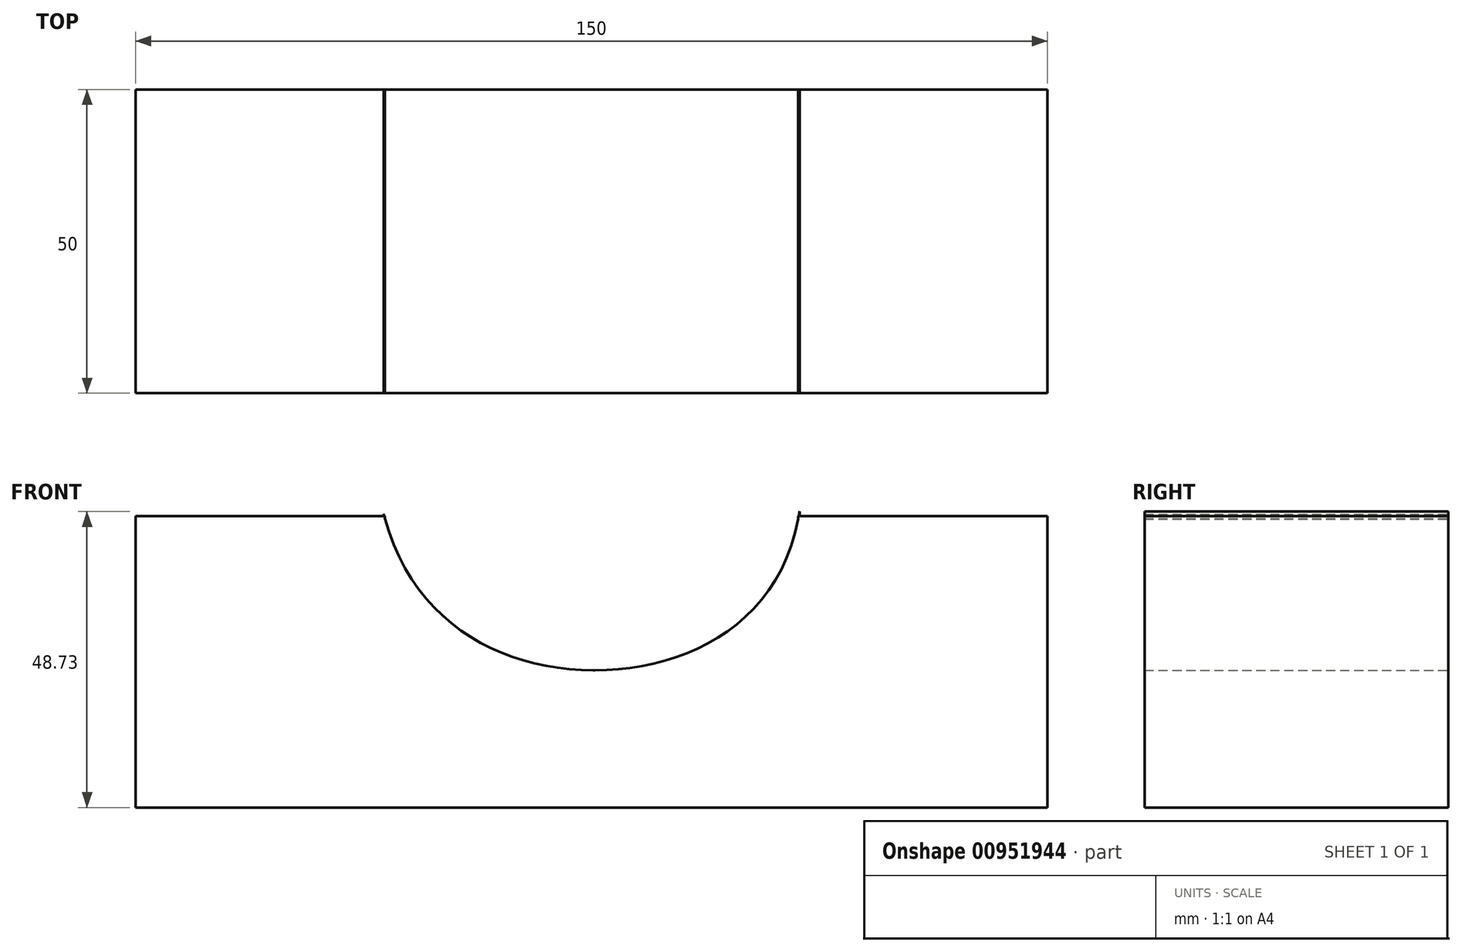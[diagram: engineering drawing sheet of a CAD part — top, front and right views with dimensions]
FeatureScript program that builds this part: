
annotation { "Feature Type Name" : "Feature", "Feature Type Description" : "" }
export const myFeature = defineFeature(function(context is Context, id is Id, definition is map)
    precondition{}
    {
        {
            var Q0;
            Q0=qCreatedBy(makeId("Front.planeOp"),FACE);
            var sketch = newSketch(context, id + "F0", { "sketchPlane" : qUnion([Q0])});
            skLineSegment(sketch, "E0", {"start": v(-75.26, 25.41) * mm, "end": v(-75.26, -22.59) * mm});
            skLineSegment(sketch, "E1", {"start": v(-75.26, -22.59) * mm, "end": v(74.74, -22.59) * mm});
            skLineSegment(sketch, "E2", {"start": v(74.74, -22.59) * mm, "end": v(74.74, 25.41) * mm});
            skLineSegment(sketch, "E3", {"start": v(74.74, 25.41) * mm, "end": v(33.74, 25.41) * mm});
            skLineSegment(sketch, "E4", {"start": v(33.74, 25.41) * mm, "end": v(33.74, 0) * mm});
            skLineSegment(sketch, "E5", {"start": v(33.74, 0) * mm, "end": v(-34.26, 0) * mm});
            skLineSegment(sketch, "E6", {"start": v(-34.26, 0) * mm, "end": v(-34.26, 25.41) * mm});
            skLineSegment(sketch, "E7", {"start": v(-34.26, 25.41) * mm, "end": v(-75.26, 25.41) * mm});
            skSolve(sketch);
        }
        {
            var Q0;
            Q0=makeQuery(id+"F0.imprint","IMPRINT",FACE,{"disambiguationData":[TD([[makeQuery(id+"F0.imprint","IMPRINT",EDGE,{"derivedFrom":sQuery(id+"F0.wireOp",EDGE,"E0")}),1.0]])]});
            extrude(context, id + "F1", {"entities" : qUnion([Q0]), "depth" : 50 * mm, "offsetDistance" : 25 * mm});
        }
        {
            var Q0;
            Q0=qCreatedBy(makeId("Front.planeOp"),FACE);
            var sketch = newSketch(context, id + "F2", { "sketchPlane" : qUnion([Q0])});
            skLineSegment(sketch, "E8", {"start": v(-34.44, 25.7) * mm, "end": v(-34.44, 0) * mm});
            skLineSegment(sketch, "E9", {"start": v(-34.44, 0) * mm, "end": v(33.96, 0) * mm});
            skLineSegment(sketch, "E10", {"start": v(33.96, 0) * mm, "end": v(33.96, 26.14) * mm});
            skFitSpline(sketch, "E11", {"points": [v(-34.44, 25.7) * mm, v(0, 0) * mm, v(33.96, 26.14) * mm], "startDerivative": vector(27.43, -107.1) * mm, "endDerivative": vector(17, 111.17) * mm});
            skSolve(sketch);
        }
        {
            var Q0;
            Q0 = qSketchRegion(id + "F2", true);
            extrude(context, id + "F3", {"entities" : qUnion([Q0]), "operationType" : NewBodyOperationType.ADD, "depth" : 50 * mm, "offsetDistance" : 25 * mm});
        }
    });
